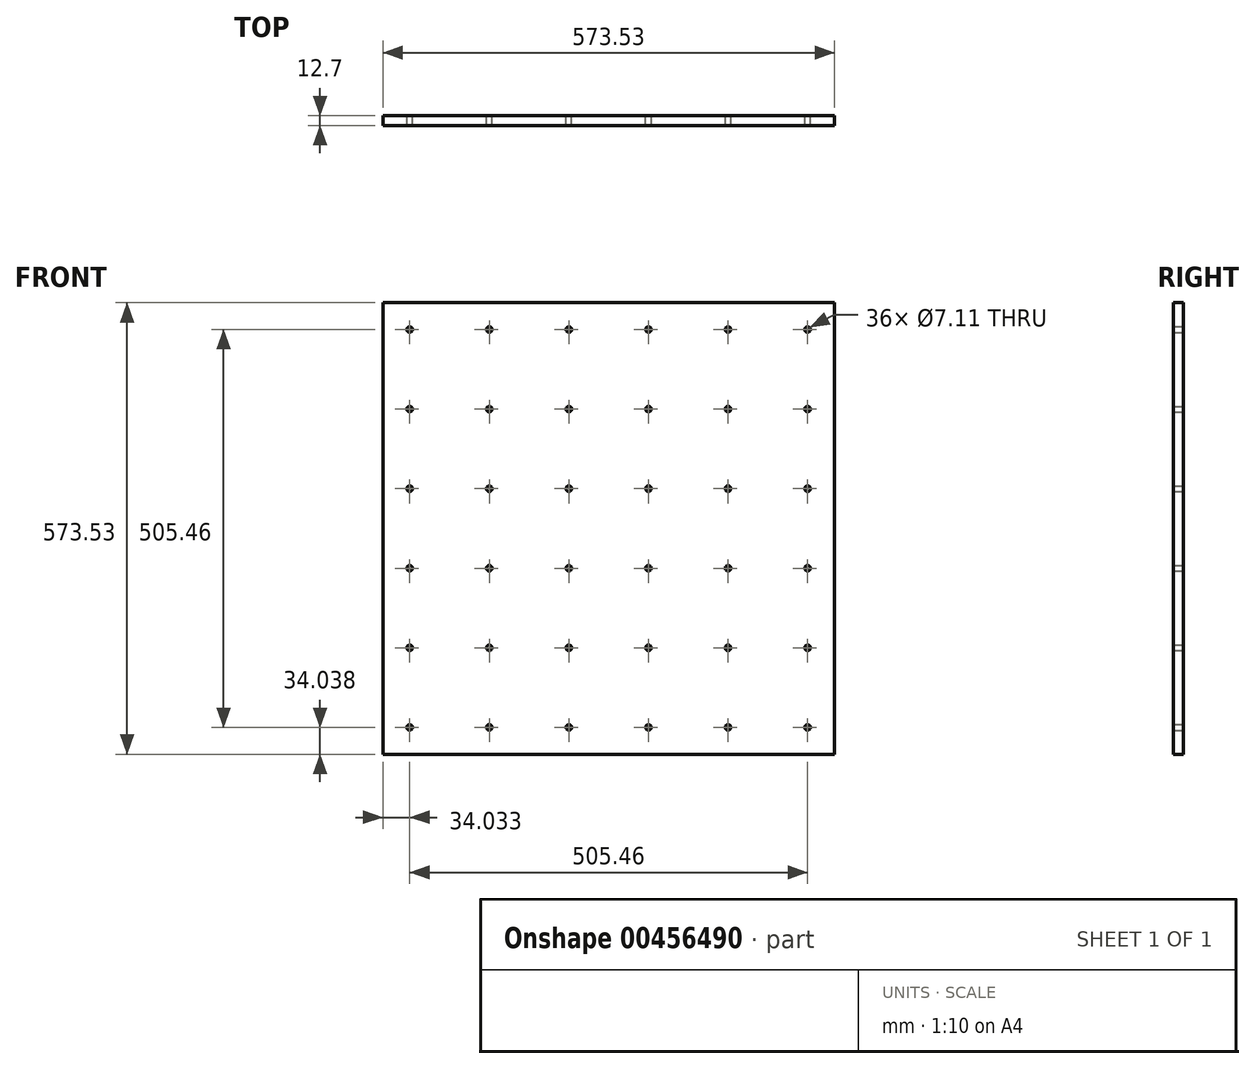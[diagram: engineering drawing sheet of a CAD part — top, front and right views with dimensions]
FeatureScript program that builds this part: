
annotation { "Feature Type Name" : "Feature", "Feature Type Description" : "" }
export const myFeature = defineFeature(function(context is Context, id is Id, definition is map)
    precondition{}
    {
        {
            var Q0;
            Q0=qCreatedBy(makeId("Front.planeOp"),FACE);
            var sketch = newSketch(context, id + "F0", { "sketchPlane" : qUnion([Q0])});
            skLineSegment(sketch, "E0.bottom", {"start": v(-169.8, 438.4) * mm, "end": v(403.73, 438.4) * mm});
            skLineSegment(sketch, "E0.top", {"start": v(-169.8, -135.13) * mm, "end": v(403.73, -135.13) * mm});
            skLineSegment(sketch, "E0.left", {"start": v(-169.8, 438.4) * mm, "end": v(-169.8, -135.13) * mm});
            skLineSegment(sketch, "E0.right", {"start": v(403.73, 438.4) * mm, "end": v(403.73, -135.13) * mm});
            skCircle(sketch, "E1", {"center": v(-135.77, 404.37) * mm, "radius": 3.56 * mm});
            skCircle(sketch, "E2", {"center": v(-135.77, 303.28) * mm, "radius": 3.56 * mm});
            skCircle(sketch, "E3", {"center": v(-135.77, 101.1) * mm, "radius": 3.56 * mm});
            skCircle(sketch, "E4", {"center": v(-135.77, 0) * mm, "radius": 3.56 * mm});
            skCircle(sketch, "E5", {"center": v(-135.77, -101.1) * mm, "radius": 3.56 * mm});
            skCircle(sketch, "E6", {"center": v(-135.77, 202.18) * mm, "radius": 3.56 * mm});
            skCircle(sketch, "E7", {"center": v(-34.67, 404.37) * mm, "radius": 3.56 * mm});
            skCircle(sketch, "E8", {"center": v(66.42, 404.37) * mm, "radius": 3.56 * mm});
            skCircle(sketch, "E9", {"center": v(167.5, 404.37) * mm, "radius": 3.56 * mm});
            skCircle(sketch, "E10", {"center": v(268.6, 404.37) * mm, "radius": 3.56 * mm});
            skCircle(sketch, "E11", {"center": v(369.7, 404.37) * mm, "radius": 3.56 * mm});
            skCircle(sketch, "E12", {"center": v(-34.67, 303.28) * mm, "radius": 3.56 * mm});
            skCircle(sketch, "E13", {"center": v(66.42, 303.28) * mm, "radius": 3.56 * mm});
            skCircle(sketch, "E14", {"center": v(167.5, 303.28) * mm, "radius": 3.56 * mm});
            skCircle(sketch, "E15", {"center": v(268.6, 303.28) * mm, "radius": 3.56 * mm});
            skCircle(sketch, "E16", {"center": v(369.7, 303.28) * mm, "radius": 3.56 * mm});
            skCircle(sketch, "E17", {"center": v(-34.67, 202.18) * mm, "radius": 3.56 * mm});
            skCircle(sketch, "E18", {"center": v(66.42, 202.18) * mm, "radius": 3.56 * mm});
            skCircle(sketch, "E19", {"center": v(167.5, 202.18) * mm, "radius": 3.56 * mm});
            skCircle(sketch, "E20", {"center": v(268.6, 202.18) * mm, "radius": 3.56 * mm});
            skCircle(sketch, "E21", {"center": v(369.7, 202.18) * mm, "radius": 3.56 * mm});
            skCircle(sketch, "E22", {"center": v(-34.67, 101.1) * mm, "radius": 3.56 * mm});
            skCircle(sketch, "E23", {"center": v(66.42, 101.1) * mm, "radius": 3.56 * mm});
            skCircle(sketch, "E24", {"center": v(167.5, 101.1) * mm, "radius": 3.56 * mm});
            skCircle(sketch, "E25", {"center": v(268.6, 101.1) * mm, "radius": 3.56 * mm});
            skCircle(sketch, "E26", {"center": v(369.7, 101.1) * mm, "radius": 3.56 * mm});
            skCircle(sketch, "E27", {"center": v(-34.67, -101.1) * mm, "radius": 3.56 * mm});
            skCircle(sketch, "E28", {"center": v(66.42, -101.1) * mm, "radius": 3.56 * mm});
            skCircle(sketch, "E29", {"center": v(167.5, -101.1) * mm, "radius": 3.56 * mm});
            skCircle(sketch, "E30", {"center": v(268.6, -101.1) * mm, "radius": 3.56 * mm});
            skCircle(sketch, "E31", {"center": v(369.7, -101.1) * mm, "radius": 3.56 * mm});
            skCircle(sketch, "E32", {"center": v(-34.67, 0) * mm, "radius": 3.56 * mm});
            skCircle(sketch, "E33", {"center": v(66.42, 0) * mm, "radius": 3.56 * mm});
            skCircle(sketch, "E34", {"center": v(167.5, 0) * mm, "radius": 3.56 * mm});
            skCircle(sketch, "E35", {"center": v(268.6, 0) * mm, "radius": 3.56 * mm});
            skCircle(sketch, "E36", {"center": v(369.7, 0) * mm, "radius": 3.56 * mm});
            skSolve(sketch);
        }
        {
            var Q0;
            Q0 = qSketchRegion(id + "F0", true);
            extrude(context, id + "F1", {"entities" : qUnion([Q0]), "depth" : 12.7 * mm, "offsetDistance" : 25.4 * mm});
        }
    });
